# Revit family: Satellite Pendant 2.25
name_source: partatom
category: Lighting Fixtures
revit_build: Autodesk Revit 2017 (Build: 20190508_0315(x64)
units: mm (PartAtom-declared; Revit-internal decimal feet)

## family parameters
Cut with Voids When Loaded = No
Host = Face
Light Source = Yes
Part Type = Normal
Room Calculation Point = No
Round Connector Dimension = Use Diameter
Shared = No

## types (1)
- Satellite Pendant 2.25
    Canopy Width = 5"
    Color Filter = 16777215
    Cost = 259 $
    Default Elevation = 0"
    Description = The Satellite Pendant 2.25” offers uncommon character from a strikingly simple form. Part of a lighting family that channels the spirit of early 20th century industrial fixtures, the Satellite Pendant 2.25” shines when combined with metal, painted, and glass shades. Assembled in our Portland, Ore. factory using ethically-sourced domestic and global components. A Schoolhouse Original.
    Dimming Lamp Color Temperature Shift = <None>
    Height = 15 1/4"
    Light Source Symbol Size = 2 1/4"
    Max Wattage = 100 W
    Primary Finishes = Natural Brass, True Black, Satin Nickel
    Product Material = Schoolhouse_Brass
    URL = https://www.schoolhouse.com
    Voltage = 120 /220V
    Width = 2 1/4"

## geometry (parser evidence)
native form markers: Sweep x3
no freeform markers — native parametric forms only
